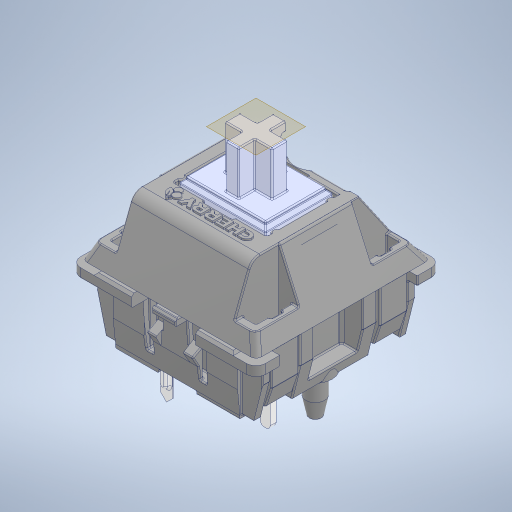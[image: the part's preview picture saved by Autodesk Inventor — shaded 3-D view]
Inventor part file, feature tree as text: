
AUTODESK INVENTOR PART (.ipt)
format: ipt  version: 2023 (Build 270158000, 158)  size: 2,601,984 bytes
history: native  units: in
note: dims shown in document units (in); Inventor stores cm internally (conversion verified against a paired STEP export)
features: extrude x8, other x7, plane x4, sketch x4, fillet x2, projected_geometry x2, chamfer x1, boolean_combine x1
ambient origin geometry x8: Origin, YZ Plane, XZ Plane, XY Plane, X Axis, Y Axis, Z Axis, Center Point
bodies: Solid1 (feature_tree), Solid7 (feature_tree), Solid8 (feature_tree), Solid9 (feature_tree), Solid10 (feature_tree)
feature tree (29):
  plane  "Work Plane1"
  sketch  "Sketch3"  dims[d11=0.0118in d15=0.1969in d16=0.0in]
  extrude  "Extrusion3"  Depth=0.1969in TaperAngle=0.0deg
  extrude  "Extrusion5"  Depth=1.5748in
  extrude  "Extrusion6"  Depth=0.3937in TaperAngle=0.0deg
  plane  "Work Plane2"
  sketch  "Sketch4"  dims[d19=0.1417in d20=0.0in d21=1.5748in]
  extrude  "Extrusion7"  Depth=0.0787in TaperAngle=0.0deg
  extrude  "Extrusion8"  Depth=0.3937in TaperAngle=0.0deg
  plane  "Work Plane3"
  extrude  "Extrusion9"  Depth=0.0787in
  plane  "Work Plane4"
  extrude  "Extrusion10"  Depth=0.0787in
  fillet  "Fillet1"  [1 undecoded]
  chamfer  "Chamfer2"  Distance=0.0059in
  extrude  "Extrusion11"  Depth=0.0787in
  fillet  "Fillet2"  Radius=0.0039in
  boolean_combine  "Combine1"
  projected_geometry  "Projected Loop3"
  other  "lid"
  projected_geometry  "Projected Loop5"
  other  "bottom"
  sketch  "Sketch7"  dims[d22=1.5748in d34=0.3937in d35=0.0in]
  sketch  "Sketch8"  dims[d36=-2.4737in d37=0.9843in d38=0.0in d48=0.3937in d49=0.0in d50=0.0059in d51=0.0059in d52=0.0in d53=0.0059in d55=0.0039in d57=0.0039in d58=0.0079in d59=0.0039in d60=0.0059in d61=0.6201in d62=0.0in d63=0.0in d64=30.0deg d66=0.4434in d67=0.7842in d68=0.0in d69=0.0in d70=0.3937in d71=0.0184in d72=0.0787in d73=45.0deg d74=0.1811in d75=0.1811in d76=0.1811in d77=0.1811in d78=0.1063in d79=0.0098in d80=0.0098in d81=0.0098in d82=0.0098in d83=0.1378in d84=0.248in d85=0.0in d86=0.0787in d87=0.0035in d17=0.0197in d18=0.0344in]
  other  "MX-solid1-F1"
  other  "MX-solid6-F6"
  other  "T-2-solid1"
  other  "T-2-solid2"
  other  "Boss-Extrude1"
note: 1 required parameter value undecoded (feature->parameter linkage not recoverable at this tier; creation-order binding heuristic only, values carry confidence <= 0.55)
